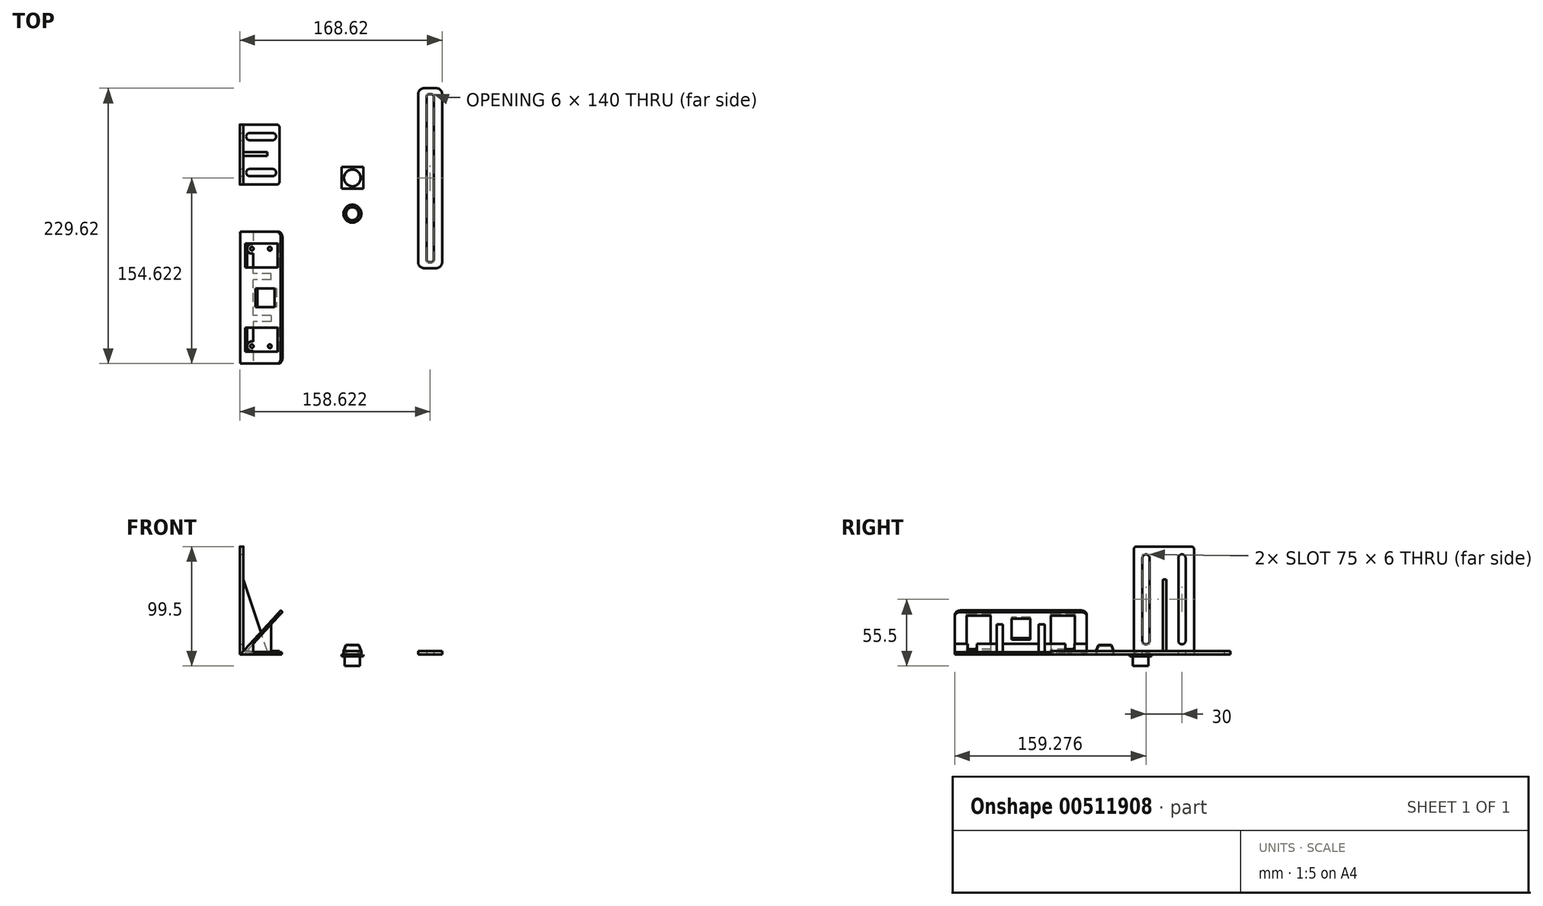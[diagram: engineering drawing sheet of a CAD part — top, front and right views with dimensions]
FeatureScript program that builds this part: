
annotation { "Feature Type Name" : "Feature", "Feature Type Description" : "" }
export const myFeature = defineFeature(function(context is Context, id is Id, definition is map)
    precondition{}
    {
        {
            var Q0;
            Q0=qCreatedBy(makeId("Top.planeOp"),FACE);
            var sketch = newSketch(context, id + "F0", { "sketchPlane" : qUnion([Q0])});
            skCircle(sketch, "E0", {"center": v(0, 0) * mm, "radius": 7 * mm});
            skSolve(sketch);
        }
        {
            var Q0;
            Q0=makeQuery(id+"F0.imprint","IMPRINT",FACE,{"disambiguationData":[TD([[makeQuery(id+"F0.imprint","IMPRINT",EDGE,{"derivedFrom":sQuery(id+"F0.wireOp",EDGE,"E0")}),1.0]])]});
            extrude(context, id + "F1", {"entities" : qUnion([Q0]), "depth" : 2.5 * mm, "offsetDistance" : 25 * mm});
        }
        {
            var Q0;
            Q0=makeQuery(id+"F1.opExtrude","CAP_EDGE",EDGE,{"disambiguationData":[OSD([sQuery(id+"F0.wireOp",EDGE,"E0")])],"isStart":false});
            fillet(context, id + "F2", {"entities" : qUnion([Q0]), "radius" : 7 * mm, "tangentPropagation" : true, "allowEdgeOverflow" : false});
        }
        {
            var Q0;
            Q0=makeQuery(id+"F1.opExtrude","CAP_FACE",FACE,{"disambiguationData":[OSD([sQuery(id+"F0.wireOp",EDGE,"E0")])],"isStart":true});
            cPlane(context, id + "F3", {"entities" : qUnion([Q0]), "cplaneType" : CPlaneType.OFFSET, "offset" : 0 * mm, "width" : 150 * mm, "height" : 150 * mm});
        }
        {
            var Q0;
            Q0=qCreatedBy(id+"F3.planeOp",FACE);
            var sketch = newSketch(context, id + "F4", { "sketchPlane" : qUnion([Q0])});
            skLineSegment(sketch, "E1.bottom", {"start": v(-9, -9) * mm, "end": v(9, -9) * mm});
            skLineSegment(sketch, "E1.top", {"start": v(-9, 9) * mm, "end": v(9, 9) * mm});
            skLineSegment(sketch, "E1.left", {"start": v(-9, -9) * mm, "end": v(-9, 9) * mm});
            skLineSegment(sketch, "E1.right", {"start": v(9, -9) * mm, "end": v(9, 9) * mm});
            skSolve(sketch);
        }
        {
            var Q0;
            Q0 = qSketchRegion(id + "F4", true);
            extrude(context, id + "F5", {"entities" : qUnion([Q0]), "operationType" : NewBodyOperationType.ADD, "depth" : 1.5 * mm, "offsetDistance" : 25 * mm});
        }
        {
            var Q0;
            Q0=makeQuery(id+"F5.opExtrude","CAP_FACE",FACE,{"disambiguationData":[OSD([sQuery(id+"F4.wireOp",EDGE,"E1.bottom"),sQuery(id+"F4.wireOp",EDGE,"E1.top"),sQuery(id+"F4.wireOp",EDGE,"E1.left"),sQuery(id+"F4.wireOp",EDGE,"E1.right")])],"isStart":false});
            cPlane(context, id + "F6", {"entities" : qUnion([Q0]), "cplaneType" : CPlaneType.OFFSET, "offset" : 0 * mm, "width" : 150 * mm, "height" : 150 * mm});
        }
        {
            var Q0;
            Q0=qCreatedBy(id+"F6.planeOp",FACE);
            var sketch = newSketch(context, id + "F7", { "sketchPlane" : qUnion([Q0])});
            skCircle(sketch, "E2", {"center": v(0, 0) * mm, "radius": 6.4 * mm});
            skSolve(sketch);
        }
        {
            var Q0;
            Q0 = qSketchRegion(id + "F7", true);
            extrude(context, id + "F8", {"entities" : qUnion([Q0]), "operationType" : NewBodyOperationType.ADD, "depth" : 8 * mm, "offsetDistance" : 25 * mm});
        }
        {
            var Q0;
            Q0=qCreatedBy(makeId("Top.planeOp"),FACE);
            var sketch = newSketch(context, id + "F9", { "sketchPlane" : qUnion([Q0])});
            skCircle(sketch, "E3", {"center": v(0, -29.84) * mm, "radius": 7.45 * mm});
            skSolve(sketch);
        }
        {
            var Q0;
            Q0 = qSketchRegion(id + "F9", true);
            extrude(context, id + "F10", {"entities" : qUnion([Q0]), "depth" : 8 * mm, "offsetDistance" : 25 * mm});
        }
        {
            var Q0;
            Q0=makeQuery(id+"F10.opExtrude","CAP_EDGE",EDGE,{"disambiguationData":[OSD([sQuery(id+"F9.wireOp",EDGE,"E3")])],"isStart":false});
            chamfer(context, id + "F11", {"entities" : qUnion([Q0]), "chamferType" : ChamferType.TWO_OFFSETS, "width1" : 2 * mm, "oppositeDirection" : false, "width2" : 5 * mm, "tangentPropagation" : true});
        }
        {
            var Q0;
            Q0=qCreatedBy(makeId("Top.planeOp"),FACE);
            var sketch = newSketch(context, id + "F12", { "sketchPlane" : qUnion([Q0])});
            skCircle(sketch, "E4", {"center": v(0, -29.84) * mm, "radius": 6.45 * mm});
            skSolve(sketch);
        }
        {
            var Q0;
            Q0 = qSketchRegion(id + "F12", true);
            extrude(context, id + "F13", {"entities" : qUnion([Q0]), "depth" : 7 * mm, "offsetDistance" : 25 * mm});
        }
        {
            var Q0;
            Q0=makeQuery(id+"F13.opExtrude","CAP_EDGE",EDGE,{"disambiguationData":[OSD([sQuery(id+"F12.wireOp",EDGE,"E4")])],"isStart":false});
            chamfer(context, id + "F14", {"entities" : qUnion([Q0]), "chamferType" : ChamferType.TWO_OFFSETS, "width1" : 1.7 * mm, "oppositeDirection" : false, "width2" : 4 * mm, "tangentPropagation" : true});
        }
        {
            var Q0;
            Q0=makeQuery(id+"F13.opExtrude","SWEPT_BODY",BODY,{"disambiguationData":[OSD([sQuery(id+"F12.wireOp",EDGE,"E4")])]});
            var Q1;
            Q1=makeQuery(id+"F10.opExtrude","SWEPT_BODY",BODY,{"disambiguationData":[OSD([sQuery(id+"F9.wireOp",EDGE,"E3")])]});
            booleanBodies(context, id + "F15", {"operationType" : BooleanOperationType.SUBTRACTION, "tools" : qUnion([Q0]), "targets" : qUnion([Q1])});
        }
        {
            var Q0;
            Q0=qCreatedBy(makeId("Top.planeOp"),FACE);
            var sketch = newSketch(context, id + "F16", { "sketchPlane" : qUnion([Q0])});
            skLineSegment(sketch, "E5.bottom", {"start": v(59.8, 74.78) * mm, "end": v(69.8, 74.78) * mm});
            skLineSegment(sketch, "E5.top", {"start": v(59.8, -75.22) * mm, "end": v(69.8, -75.22) * mm});
            skLineSegment(sketch, "E5.left", {"start": v(54.8, 69.78) * mm, "end": v(54.8, -70.22) * mm});
            skLineSegment(sketch, "E5.right", {"start": v(74.8, 69.78) * mm, "end": v(74.8, -70.22) * mm});
            skPoint(sketch, "E6.visualSharp", {"position": v(54.8, 74.78) * mm});
            skArc(sketch, "E6.filletArc", {"start": v(59.8, 74.78) * mm, "mid": v(56.27, 73.32) * mm, "end": v(54.8, 69.78) * mm});
            skPoint(sketch, "E7.visualSharp", {"position": v(74.8, 74.78) * mm});
            skArc(sketch, "E7.filletArc", {"start": v(74.8, 69.78) * mm, "mid": v(73.34, 73.32) * mm, "end": v(69.8, 74.78) * mm});
            skPoint(sketch, "E8.visualSharp", {"position": v(54.8, -75.22) * mm});
            skArc(sketch, "E8.filletArc", {"start": v(54.8, -70.22) * mm, "mid": v(56.27, -73.75) * mm, "end": v(59.8, -75.22) * mm});
            skPoint(sketch, "E9.visualSharp", {"position": v(74.8, -75.22) * mm});
            skArc(sketch, "E9.filletArc", {"start": v(69.8, -75.22) * mm, "mid": v(73.34, -73.75) * mm, "end": v(74.8, -70.22) * mm});
            skLineSegment(sketch, "E10.bottom", {"start": v(63.8, 69.78) * mm, "end": v(65.8, 69.78) * mm});
            skLineSegment(sketch, "E10.top", {"start": v(63.8, -70.22) * mm, "end": v(65.8, -70.22) * mm});
            skLineSegment(sketch, "E10.left", {"start": v(61.8, 67.78) * mm, "end": v(61.8, -68.22) * mm});
            skLineSegment(sketch, "E10.right", {"start": v(67.8, 67.78) * mm, "end": v(67.8, -68.22) * mm});
            skPoint(sketch, "E11.visualSharp", {"position": v(61.8, 69.78) * mm});
            skArc(sketch, "E11.filletArc", {"start": v(63.8, 69.78) * mm, "mid": v(62.39, 69.2) * mm, "end": v(61.8, 67.78) * mm});
            skPoint(sketch, "E12.visualSharp", {"position": v(61.8, -70.22) * mm});
            skArc(sketch, "E12.filletArc", {"start": v(61.8, -68.22) * mm, "mid": v(62.39, -69.63) * mm, "end": v(63.8, -70.22) * mm});
            skPoint(sketch, "E13.visualSharp", {"position": v(67.8, -70.22) * mm});
            skArc(sketch, "E13.filletArc", {"start": v(65.8, -70.22) * mm, "mid": v(67.22, -69.63) * mm, "end": v(67.8, -68.22) * mm});
            skPoint(sketch, "E14.visualSharp", {"position": v(67.8, 69.78) * mm});
            skArc(sketch, "E14.filletArc", {"start": v(67.8, 67.78) * mm, "mid": v(67.22, 69.2) * mm, "end": v(65.8, 69.78) * mm});
            skSolve(sketch);
        }
        {
            var Q0;
            Q0 = qSketchRegion(id + "F16", true);
            extrude(context, id + "F17", {"entities" : qUnion([Q0]), "depth" : 3 * mm, "offsetDistance" : 25 * mm});
        }
        {
            var Q0;
            Q0=qCreatedBy(makeId("Top.planeOp"),FACE);
            var sketch = newSketch(context, id + "F18", { "sketchPlane" : qUnion([Q0])});
            skLineSegment(sketch, "E15.bottom", {"start": v(-90.82, 44.44) * mm, "end": v(-62.82, 44.44) * mm});
            skLineSegment(sketch, "E15.top", {"start": v(-90.82, -5.56) * mm, "end": v(-62.82, -5.56) * mm});
            skLineSegment(sketch, "E15.left", {"start": v(-90.82, 44.44) * mm, "end": v(-90.82, -5.56) * mm});
            skLineSegment(sketch, "E15.right", {"start": v(-60.82, 42.44) * mm, "end": v(-60.82, -3.56) * mm});
            skPoint(sketch, "E16.visualSharp", {"position": v(-60.82, 44.44) * mm});
            skArc(sketch, "E16.filletArc", {"start": v(-60.82, 42.44) * mm, "mid": v(-61.4, 43.85) * mm, "end": v(-62.82, 44.44) * mm});
            skPoint(sketch, "E17.visualSharp", {"position": v(-60.82, -5.56) * mm});
            skArc(sketch, "E17.filletArc", {"start": v(-62.82, -5.56) * mm, "mid": v(-61.4, -4.98) * mm, "end": v(-60.82, -3.56) * mm});
            skLineSegment(sketch, "E18.bottom", {"start": v(-101.44, 55.6) * mm, "end": v(-90.82, 55.6) * mm, "construction": true});
            skLineSegment(sketch, "E18.top", {"start": v(-101.44, -19.09) * mm, "end": v(-90.82, -19.09) * mm, "construction": true});
            skLineSegment(sketch, "E18.left", {"start": v(-101.44, 55.6) * mm, "end": v(-101.44, -19.09) * mm, "construction": true});
            skLineSegment(sketch, "E18.right", {"start": v(-90.82, 55.6) * mm, "end": v(-90.82, -19.09) * mm, "construction": true});
            skSolve(sketch);
        }
        {
            var Q0;
            Q0 = qSketchRegion(id + "F18", true);
            extrude(context, id + "F19", {"entities" : qUnion([Q0]), "depth" : 3 * mm, "offsetDistance" : 25 * mm});
        }
        {
            var Q0;
            Q0=qCreatedBy(makeId("Top.planeOp"),FACE);
            var sketch = newSketch(context, id + "F20", { "sketchPlane" : qUnion([Q0])});
            skLineSegment(sketch, "E19.bottom", {"start": v(-93.82, 44.44) * mm, "end": v(-90.82, 44.44) * mm});
            skLineSegment(sketch, "E19.top", {"start": v(-93.82, -5.56) * mm, "end": v(-90.82, -5.56) * mm});
            skLineSegment(sketch, "E19.left", {"start": v(-93.82, 44.44) * mm, "end": v(-93.82, -5.56) * mm});
            skLineSegment(sketch, "E19.right", {"start": v(-90.82, 44.44) * mm, "end": v(-90.82, -5.56) * mm});
            skSolve(sketch);
        }
        {
            var Q0;
            Q0 = qSketchRegion(id + "F20", true);
            extrude(context, id + "F21", {"entities" : qUnion([Q0]), "operationType" : NewBodyOperationType.ADD, "depth" : 90 * mm, "offsetDistance" : 25 * mm});
        }
        {
            var Q0;
            Q0=makeQuery(id+"F21.opExtrude","CAP_EDGE",EDGE,{"disambiguationData":[OSD([sQuery(id+"F20.wireOp",EDGE,"E19.top")])],"isStart":false});
            var Q1;
            Q1=makeQuery(id+"F21.opExtrude","CAP_EDGE",EDGE,{"disambiguationData":[OSD([sQuery(id+"F20.wireOp",EDGE,"E19.bottom")])],"isStart":false});
            fillet(context, id + "F22", {"entities" : qUnion([Q0, Q1]), "radius" : 2 * mm, "tangentPropagation" : true, "allowEdgeOverflow" : false});
        }
        {
            var Q0;
            Q0=makeQuery(id+"F19.opExtrude","CAP_FACE",FACE,{"disambiguationData":[OSD([sQuery(id+"F18.wireOp",EDGE,"E15.bottom"),sQuery(id+"F18.wireOp",EDGE,"E15.top"),sQuery(id+"F18.wireOp",EDGE,"E15.left"),sQuery(id+"F18.wireOp",EDGE,"E15.right"),sQuery(id+"F18.wireOp",EDGE,"E16.filletArc"),sQuery(id+"F18.wireOp",EDGE,"E17.filletArc")])],"isStart":false});
            var sketch = newSketch(context, id + "F23", { "sketchPlane" : qUnion([Q0])});
            skLineSegment(sketch, "E20.bottom", {"start": v(-85.49, 37.44) * mm, "end": v(-66.49, 37.44) * mm});
            skLineSegment(sketch, "E20.top", {"start": v(-85.49, 31.44) * mm, "end": v(-66.49, 31.44) * mm});
            skLineSegment(sketch, "E20.left", {"start": v(-88.49, 34.44) * mm, "end": v(-88.49, 34.44) * mm});
            skLineSegment(sketch, "E20.right", {"start": v(-63.49, 34.44) * mm, "end": v(-63.49, 34.44) * mm});
            skPoint(sketch, "E21.visualSharp", {"position": v(-88.49, 37.44) * mm});
            skArc(sketch, "E21.filletArc", {"start": v(-85.49, 37.44) * mm, "mid": v(-87.6, 36.56) * mm, "end": v(-88.49, 34.44) * mm});
            skPoint(sketch, "E22.visualSharp", {"position": v(-88.49, 31.44) * mm});
            skArc(sketch, "E22.filletArc", {"start": v(-88.49, 34.44) * mm, "mid": v(-87.6, 32.31) * mm, "end": v(-85.49, 31.44) * mm});
            skPoint(sketch, "E23.visualSharp", {"position": v(-63.49, 31.44) * mm});
            skArc(sketch, "E23.filletArc", {"start": v(-66.49, 31.44) * mm, "mid": v(-64.37, 32.31) * mm, "end": v(-63.49, 34.44) * mm});
            skPoint(sketch, "E24.visualSharp", {"position": v(-63.49, 37.44) * mm});
            skArc(sketch, "E24.filletArc", {"start": v(-63.49, 34.44) * mm, "mid": v(-64.37, 36.56) * mm, "end": v(-66.49, 37.44) * mm});
            skLineSegment(sketch, "E25.bottom", {"start": v(-85.49, 7.44) * mm, "end": v(-66.49, 7.44) * mm});
            skLineSegment(sketch, "E25.top", {"start": v(-85.49, 1.44) * mm, "end": v(-66.49, 1.44) * mm});
            skLineSegment(sketch, "E25.left", {"start": v(-88.49, 4.44) * mm, "end": v(-88.49, 4.44) * mm});
            skLineSegment(sketch, "E25.right", {"start": v(-63.49, 4.44) * mm, "end": v(-63.49, 4.44) * mm});
            skPoint(sketch, "E26.visualSharp", {"position": v(-88.49, 7.44) * mm});
            skArc(sketch, "E26.filletArc", {"start": v(-85.49, 7.44) * mm, "mid": v(-87.61, 6.56) * mm, "end": v(-88.49, 4.44) * mm});
            skPoint(sketch, "E27.visualSharp", {"position": v(-88.49, 1.44) * mm});
            skArc(sketch, "E27.filletArc", {"start": v(-88.49, 4.44) * mm, "mid": v(-87.61, 2.31) * mm, "end": v(-85.49, 1.44) * mm});
            skPoint(sketch, "E28.visualSharp", {"position": v(-63.49, 1.44) * mm});
            skArc(sketch, "E28.filletArc", {"start": v(-66.49, 1.44) * mm, "mid": v(-64.37, 2.31) * mm, "end": v(-63.49, 4.44) * mm});
            skPoint(sketch, "E29.visualSharp", {"position": v(-63.49, 7.44) * mm});
            skArc(sketch, "E29.filletArc", {"start": v(-63.49, 4.44) * mm, "mid": v(-64.37, 6.56) * mm, "end": v(-66.49, 7.44) * mm});
            skSolve(sketch);
        }
        {
            var Q0;
            Q0 = qSketchRegion(id + "F23", true);
            extrude(context, id + "F24", {"entities" : qUnion([Q0]), "operationType" : NewBodyOperationType.REMOVE, "oppositeDirection" : true, "depth" : 25 * mm, "offsetDistance" : 25 * mm});
        }
        {
            var Q0;
            Q0=makeQuery(id+"F21.opExtrude","SWEPT_FACE",FACE,{"disambiguationData":[OSD([sQuery(id+"F20.wireOp",EDGE,"E19.right")])]});
            var sketch = newSketch(context, id + "F25", { "sketchPlane" : qUnion([Q0])});
            skLineSegment(sketch, "E30.bottom", {"start": v(34.44, 83.5) * mm, "end": v(34.44, 83.5) * mm});
            skLineSegment(sketch, "E30.top", {"start": v(34.44, 8.5) * mm, "end": v(34.44, 8.5) * mm});
            skLineSegment(sketch, "E30.left", {"start": v(31.44, 80.5) * mm, "end": v(31.44, 11.5) * mm});
            skLineSegment(sketch, "E30.right", {"start": v(37.44, 80.5) * mm, "end": v(37.44, 11.5) * mm});
            skPoint(sketch, "E31.visualSharp", {"position": v(31.44, 83.5) * mm});
            skArc(sketch, "E31.filletArc", {"start": v(34.44, 83.5) * mm, "mid": v(32.31, 82.62) * mm, "end": v(31.44, 80.5) * mm});
            skPoint(sketch, "E32.visualSharp", {"position": v(31.44, 8.5) * mm});
            skArc(sketch, "E32.filletArc", {"start": v(31.44, 11.5) * mm, "mid": v(32.31, 9.38) * mm, "end": v(34.44, 8.5) * mm});
            skPoint(sketch, "E33.visualSharp", {"position": v(37.44, 83.5) * mm});
            skArc(sketch, "E33.filletArc", {"start": v(37.44, 80.5) * mm, "mid": v(36.56, 82.62) * mm, "end": v(34.44, 83.5) * mm});
            skPoint(sketch, "E34.visualSharp", {"position": v(37.44, 8.5) * mm});
            skArc(sketch, "E34.filletArc", {"start": v(34.44, 8.5) * mm, "mid": v(36.56, 9.38) * mm, "end": v(37.44, 11.5) * mm});
            skLineSegment(sketch, "E35.bottom", {"start": v(49.07, 61.34) * mm, "end": v(49.07, 61.34) * mm});
            skLineSegment(sketch, "E35.top", {"start": v(49.07, -13.66) * mm, "end": v(49.07, -13.66) * mm});
            skLineSegment(sketch, "E35.left", {"start": v(1.44, 80.5) * mm, "end": v(1.44, 11.5) * mm});
            skLineSegment(sketch, "E35.right", {"start": v(7.44, 80.5) * mm, "end": v(7.44, 11.5) * mm});
            skPoint(sketch, "E36.visualSharp", {"position": v(1.44, 83.5) * mm});
            skArc(sketch, "E36.filletArc", {"start": v(4.44, 83.5) * mm, "mid": v(2.31, 82.62) * mm, "end": v(1.44, 80.5) * mm});
            skPoint(sketch, "E37.visualSharp", {"position": v(1.44, 8.5) * mm});
            skArc(sketch, "E37.filletArc", {"start": v(1.44, 11.5) * mm, "mid": v(2.31, 9.38) * mm, "end": v(4.44, 8.5) * mm});
            skPoint(sketch, "E38.visualSharp", {"position": v(7.44, 83.5) * mm});
            skArc(sketch, "E38.filletArc", {"start": v(7.44, 80.5) * mm, "mid": v(6.56, 82.62) * mm, "end": v(4.44, 83.5) * mm});
            skPoint(sketch, "E39.visualSharp", {"position": v(7.44, 8.5) * mm});
            skArc(sketch, "E39.filletArc", {"start": v(4.44, 8.5) * mm, "mid": v(6.56, 9.38) * mm, "end": v(7.44, 11.5) * mm});
            skSolve(sketch);
        }
        {
            var Q0;
            Q0 = qSketchRegion(id + "F25", true);
            extrude(context, id + "F26", {"entities" : qUnion([Q0]), "operationType" : NewBodyOperationType.REMOVE, "oppositeDirection" : true, "depth" : 25 * mm, "offsetDistance" : 25 * mm});
        }
        {
            var Q0;
            Q0=makeQuery(id+"F29.boolean.opBoolean","MERGE",FACE,{"derivedFrom":[makeQuery(id+"F21.boolean.opBoolean","MERGE",FACE,{"derivedFrom":[makeQuery(id+"F19.opExtrude","SWEPT_FACE",FACE,{"disambiguationData":[OSD([sQuery(id+"F18.wireOp",EDGE,"E15.top")])]}),makeQuery(id+"F21.opExtrude","SWEPT_FACE",FACE,{"disambiguationData":[OSD([sQuery(id+"F20.wireOp",EDGE,"E19.top")])]})]}),makeQuery(id+"F29.opExtrude","CAP_FACE",FACE,{"disambiguationData":[OSD([sQuery(id+"F28.wireOp",EDGE,"E40"),sQuery(id+"F28.wireOp",EDGE,"E41"),sQuery(id+"F28.wireOp",EDGE,"E42")])],"isStart":true})]});
            cPlane(context, id + "F27", {"entities" : qUnion([Q0]), "cplaneType" : CPlaneType.OFFSET, "offset" : 24 * mm, "oppositeDirection" : true, "width" : 150 * mm, "height" : 150 * mm});
        }
        {
            var Q0;
            Q0=qCreatedBy(id+"F27.planeOp",FACE);
            var sketch = newSketch(context, id + "F28", { "sketchPlane" : qUnion([Q0])});
            skLineSegment(sketch, "E40", {"start": v(-90.82, 62.64) * mm, "end": v(-90.82, 3) * mm});
            skLineSegment(sketch, "E41", {"start": v(-90.82, 3) * mm, "end": v(-70.95, 3) * mm});
            skLineSegment(sketch, "E42", {"start": v(-70.95, 3) * mm, "end": v(-90.82, 62.64) * mm});
            skSolve(sketch);
        }
        {
            var Q0;
            Q0=makeQuery(id+"F28.imprint","IMPRINT",FACE,{"disambiguationData":[TD([[makeQuery(id+"F28.imprint","IMPRINT",EDGE,{"derivedFrom":sQuery(id+"F28.wireOp",EDGE,"E40")}),1.0]])]});
            extrude(context, id + "F29", {"entities" : qUnion([Q0]), "operationType" : NewBodyOperationType.ADD, "oppositeDirection" : true, "depth" : 3 * mm, "offsetDistance" : 25 * mm});
        }
        {
            var Q0;
            Q0=qCreatedBy(makeId("Top.planeOp"),FACE);
            var sketch = newSketch(context, id + "F30", { "sketchPlane" : qUnion([Q0])});
            skLineSegment(sketch, "E43.bottom", {"start": v(-88.77, -44.84) * mm, "end": v(-63.77, -44.84) * mm});
            skLineSegment(sketch, "E43.top", {"start": v(-88.77, -154.84) * mm, "end": v(-63.77, -154.84) * mm});
            skLineSegment(sketch, "E43.left", {"start": v(-88.77, -44.84) * mm, "end": v(-88.77, -154.84) * mm});
            skLineSegment(sketch, "E43.right", {"start": v(-58.77, -49.84) * mm, "end": v(-58.77, -149.84) * mm});
            skPoint(sketch, "E44.visualSharp", {"position": v(-58.77, -44.84) * mm});
            skArc(sketch, "E44.filletArc", {"start": v(-58.77, -49.84) * mm, "mid": v(-60.23, -46.3) * mm, "end": v(-63.77, -44.84) * mm});
            skPoint(sketch, "E45.visualSharp", {"position": v(-58.77, -154.84) * mm});
            skArc(sketch, "E45.filletArc", {"start": v(-63.77, -154.84) * mm, "mid": v(-60.23, -153.38) * mm, "end": v(-58.77, -149.84) * mm});
            skSolve(sketch);
        }
        {
            var Q0;
            Q0 = qSketchRegion(id + "F30", true);
            extrude(context, id + "F31", {"entities" : qUnion([Q0]), "depth" : 2 * mm, "offsetDistance" : 25 * mm});
        }
        {
            var Q0;
            Q0=makeQuery(id+"F31.opExtrude","SWEPT_FACE",FACE,{"disambiguationData":[OSD([sQuery(id+"F30.wireOp",EDGE,"E43.top")])]});
            var sketch = newSketch(context, id + "F32", { "sketchPlane" : qUnion([Q0])});
            skLineSegment(sketch, "E46", {"start": v(-88.77, 2) * mm, "end": v(-58.2, 35.45) * mm});
            skLineSegment(sketch, "E47", {"start": v(-58.2, 35.45) * mm, "end": v(-59.67, 36.8) * mm});
            skLineSegment(sketch, "E48", {"start": v(-59.67, 36.8) * mm, "end": v(-93.3, 0) * mm});
            skLineSegment(sketch, "E49", {"start": v(-93.3, 0) * mm, "end": v(-88.77, 0) * mm});
            skLineSegment(sketch, "E50", {"start": v(-88.77, 0) * mm, "end": v(-88.77, 2) * mm});
            skSolve(sketch);
        }
        {
            var Q0;
            Q0 = qSketchRegion(id + "F32", true);
            extrude(context, id + "F33", {"entities" : qUnion([Q0]), "operationType" : NewBodyOperationType.ADD, "oppositeDirection" : true, "depth" : 110 * mm, "offsetDistance" : 25 * mm});
        }
        {
            var Q0;
            Q0=makeQuery(id+"F33.opExtrude","CAP_EDGE",EDGE,{"disambiguationData":[OSD([sQuery(id+"F32.wireOp",EDGE,"E47")])],"isStart":true});
            var Q1;
            Q1=makeQuery(id+"F33.opExtrude","CAP_EDGE",EDGE,{"disambiguationData":[OSD([sQuery(id+"F32.wireOp",EDGE,"E47")])],"isStart":false});
            fillet(context, id + "F34", {"entities" : qUnion([Q0, Q1]), "radius" : 5 * mm, "tangentPropagation" : true, "allowEdgeOverflow" : false});
        }
        {
            var Q0;
            Q0=makeQuery(id+"F33.boolean.opBoolean","MERGE",FACE,{"derivedFrom":[makeQuery(id+"F31.opExtrude","SWEPT_FACE",FACE,{"disambiguationData":[OSD([sQuery(id+"F30.wireOp",EDGE,"E43.top")])]}),makeQuery(id+"F33.opExtrude","CAP_FACE",FACE,{"disambiguationData":[OSD([sQuery(id+"F32.wireOp",EDGE,"E46"),sQuery(id+"F32.wireOp",EDGE,"E47"),sQuery(id+"F32.wireOp",EDGE,"E48"),sQuery(id+"F32.wireOp",EDGE,"E49"),sQuery(id+"F32.wireOp",EDGE,"E50")])],"isStart":true})]});
            var sketch = newSketch(context, id + "F35", { "sketchPlane" : qUnion([Q0])});
            skLineSegment(sketch, "E51", {"start": v(-88.77, 2) * mm, "end": v(-82.5, 8.86) * mm});
            skLineSegment(sketch, "E52", {"start": v(-82.5, 8.86) * mm, "end": v(-82.5, 2) * mm});
            skLineSegment(sketch, "E53", {"start": v(-82.5, 2) * mm, "end": v(-88.77, 2) * mm});
            skSolve(sketch);
        }
        {
            var Q0;
            Q0 = qSketchRegion(id + "F35", true);
            extrude(context, id + "F36", {"entities" : qUnion([Q0]), "operationType" : NewBodyOperationType.ADD, "oppositeDirection" : true, "depth" : 110 * mm, "offsetDistance" : 25 * mm});
        }
        {
            var Q0;
            Q0=qCreatedBy(makeId("Top.planeOp"),FACE);
            cPlane(context, id + "F37", {"entities" : qUnion([Q0]), "cplaneType" : CPlaneType.OFFSET, "offset" : 50 * mm, "width" : 150 * mm, "height" : 150 * mm});
        }
        {
            var Q0;
            Q0=qCreatedBy(id+"F37.planeOp",FACE);
            var sketch = newSketch(context, id + "F38", { "sketchPlane" : qUnion([Q0])});
            skPoint(sketch, "E54", {"position": v(-68.77, -59.07) * mm});
            skPoint(sketch, "E55", {"position": v(-83.77, -59.07) * mm});
            skPoint(sketch, "E56", {"position": v(-68.77, -140.34) * mm});
            skPoint(sketch, "E57", {"position": v(-83.77, -140.34) * mm});
            skSolve(sketch);
        }
        {
            var Q0;
            Q0=sQuery(id+"F38.wireOp",VERTEX,"E57");
            var Q1;
            Q1=sQuery(id+"F38.wireOp",VERTEX,"E56");
            var Q2;
            Q2=sQuery(id+"F38.wireOp",VERTEX,"E55");
            var Q3;
            Q3=sQuery(id+"F38.wireOp",VERTEX,"E54");
            var Q4;
            Q4=makeQuery(id+"F31.opExtrude","SWEPT_BODY",BODY,{"disambiguationData":[OSD([sQuery(id+"F30.wireOp",EDGE,"E43.bottom"),sQuery(id+"F30.wireOp",EDGE,"E43.top"),sQuery(id+"F30.wireOp",EDGE,"E43.left"),sQuery(id+"F30.wireOp",EDGE,"E43.right"),sQuery(id+"F30.wireOp",EDGE,"E44.filletArc"),sQuery(id+"F30.wireOp",EDGE,"E45.filletArc")])]});
            hole(context, id + "F39", {"style" : HoleStyle.SIMPLE, "endStyle" : HoleEndStyle.BLIND, "holeDiameter" : 3 * mm, "holeDepth" : 50 * mm, "tappedDepth" : 12 * mm, "tapClearance" : 3, "locations" : qUnion([Q0, Q1, Q2, Q3]), "scope" : qUnion([Q4])});
        }
        {
            var Q0;
            Q0=qCreatedBy(id+"F37.planeOp",FACE);
            var sketch = newSketch(context, id + "F40", { "sketchPlane" : qUnion([Q0])});
            skPoint(sketch, "E58", {"position": v(-68.77, -59.07) * mm});
            skPoint(sketch, "E59", {"position": v(-83.77, -59.07) * mm});
            skPoint(sketch, "E60", {"position": v(-68.77, -140.34) * mm});
            skPoint(sketch, "E61", {"position": v(-83.77, -140.34) * mm});
            skSolve(sketch);
        }
        {
            var Q0;
            Q0=sQuery(id+"F40.wireOp",VERTEX,"E61");
            var Q1;
            Q1=sQuery(id+"F40.wireOp",VERTEX,"E60");
            var Q2;
            Q2=sQuery(id+"F40.wireOp",VERTEX,"E58");
            var Q3;
            Q3=sQuery(id+"F40.wireOp",VERTEX,"E59");
            var Q4;
            Q4=makeQuery(id+"F31.opExtrude","SWEPT_BODY",BODY,{"disambiguationData":[OSD([sQuery(id+"F30.wireOp",EDGE,"E43.bottom"),sQuery(id+"F30.wireOp",EDGE,"E43.top"),sQuery(id+"F30.wireOp",EDGE,"E43.left"),sQuery(id+"F30.wireOp",EDGE,"E43.right"),sQuery(id+"F30.wireOp",EDGE,"E44.filletArc"),sQuery(id+"F30.wireOp",EDGE,"E45.filletArc")])]});
            hole(context, id + "F41", {"style" : HoleStyle.SIMPLE, "endStyle" : HoleEndStyle.BLIND, "holeDiameter" : 8 * mm, "holeDepth" : 19 * mm, "tappedDepth" : 12 * mm, "tapClearance" : 3, "locations" : qUnion([Q0, Q1, Q2, Q3]), "scope" : qUnion([Q4])});
        }
        {
            var Q0;
            Q0=makeQuery(id+"F33.boolean.opBoolean","MERGE",FACE,{"derivedFrom":[makeQuery(id+"F31.opExtrude","CAP_FACE",FACE,{"disambiguationData":[OSD([sQuery(id+"F30.wireOp",EDGE,"E43.bottom"),sQuery(id+"F30.wireOp",EDGE,"E43.top"),sQuery(id+"F30.wireOp",EDGE,"E43.left"),sQuery(id+"F30.wireOp",EDGE,"E43.right"),sQuery(id+"F30.wireOp",EDGE,"E44.filletArc"),sQuery(id+"F30.wireOp",EDGE,"E45.filletArc")])],"isStart":true}),makeQuery(id+"F33.opExtrude","SWEPT_FACE",FACE,{"disambiguationData":[OSD([sQuery(id+"F32.wireOp",EDGE,"E49")])]})]});
            var sketch = newSketch(context, id + "F42", { "sketchPlane" : qUnion([Q0])});
            skCircle(sketch, "E62", {"center": v(-83.77, 59.07) * mm, "radius": 4 * mm});
            skCircle(sketch, "E63", {"center": v(-83.77, 140.34) * mm, "radius": 4 * mm});
            skSolve(sketch);
        }
        {
            var Q0;
            Q0 = qSketchRegion(id + "F42", true);
            extrude(context, id + "F43", {"entities" : qUnion([Q0]), "operationType" : NewBodyOperationType.ADD, "oppositeDirection" : true, "depth" : 2 * mm, "offsetDistance" : 25 * mm});
        }
        {
            var Q0;
            Q0=makeQuery(id+"F43.boolean.opBoolean","MERGE",FACE,{"derivedFrom":[makeQuery(id+"F31.opExtrude","CAP_FACE",FACE,{"disambiguationData":[OSD([sQuery(id+"F30.wireOp",EDGE,"E43.bottom"),sQuery(id+"F30.wireOp",EDGE,"E43.top"),sQuery(id+"F30.wireOp",EDGE,"E43.left"),sQuery(id+"F30.wireOp",EDGE,"E43.right"),sQuery(id+"F30.wireOp",EDGE,"E44.filletArc"),sQuery(id+"F30.wireOp",EDGE,"E45.filletArc")])],"isStart":false}),makeQuery(id+"F43.opExtrude","CAP_FACE",FACE,{"disambiguationData":[OSD([sQuery(id+"F42.wireOp",EDGE,"E62")])],"isStart":false}),makeQuery(id+"F43.opExtrude","CAP_FACE",FACE,{"disambiguationData":[OSD([sQuery(id+"F42.wireOp",EDGE,"E63")])],"isStart":false})]});
            var sketch = newSketch(context, id + "F44", { "sketchPlane" : qUnion([Q0])});
            skPoint(sketch, "E64", {"position": v(-83.77, -59.07) * mm});
            skPoint(sketch, "E65", {"position": v(-83.77, -140.34) * mm});
            skSolve(sketch);
        }
        {
            var Q0;
            Q0=sQuery(id+"F44.wireOp",VERTEX,"E64");
            var Q1;
            Q1=sQuery(id+"F44.wireOp",VERTEX,"E65");
            var Q2;
            Q2=makeQuery(id+"F31.opExtrude","SWEPT_BODY",BODY,{"disambiguationData":[OSD([sQuery(id+"F30.wireOp",EDGE,"E43.bottom"),sQuery(id+"F30.wireOp",EDGE,"E43.top"),sQuery(id+"F30.wireOp",EDGE,"E43.left"),sQuery(id+"F30.wireOp",EDGE,"E43.right"),sQuery(id+"F30.wireOp",EDGE,"E44.filletArc"),sQuery(id+"F30.wireOp",EDGE,"E45.filletArc")])]});
            hole(context, id + "F45", {"style" : HoleStyle.SIMPLE, "endStyle" : HoleEndStyle.BLIND, "holeDiameter" : 3 * mm, "holeDepth" : 19 * mm, "tappedDepth" : 12 * mm, "tapClearance" : 3, "locations" : qUnion([Q0, Q1]), "scope" : qUnion([Q2])});
        }
        {
            var Q0;
            Q0=makeQuery(id+"F33.opExtrude","SWEPT_FACE",FACE,{"disambiguationData":[OSD([sQuery(id+"F32.wireOp",EDGE,"E48")])]});
            cPlane(context, id + "F46", {"entities" : qUnion([Q0]), "cplaneType" : CPlaneType.OFFSET, "offset" : 25 * mm, "width" : 150 * mm, "height" : 150 * mm});
        }
        {
            var Q0;
            Q0=qCreatedBy(id+"F46.planeOp",FACE);
            var sketch = newSketch(context, id + "F47", { "sketchPlane" : qUnion([Q0])});
            skLineSegment(sketch, "E66.bottom", {"start": v(54.84, -16.95) * mm, "end": v(74.84, -16.95) * mm});
            skLineSegment(sketch, "E66.top", {"start": v(54.84, -56.95) * mm, "end": v(74.84, -56.95) * mm});
            skLineSegment(sketch, "E66.left", {"start": v(54.84, -16.95) * mm, "end": v(54.84, -56.95) * mm});
            skLineSegment(sketch, "E66.right", {"start": v(74.84, -16.95) * mm, "end": v(74.84, -56.95) * mm});
            skLineSegment(sketch, "E67.bottom", {"start": v(124.84, -16.95) * mm, "end": v(144.84, -16.95) * mm});
            skLineSegment(sketch, "E67.top", {"start": v(124.84, -56.95) * mm, "end": v(144.84, -56.95) * mm});
            skLineSegment(sketch, "E67.left", {"start": v(124.84, -16.95) * mm, "end": v(124.84, -56.95) * mm});
            skLineSegment(sketch, "E67.right", {"start": v(144.84, -16.95) * mm, "end": v(144.84, -56.95) * mm});
            skLineSegment(sketch, "E68.bottom", {"start": v(92.04, -20.68) * mm, "end": v(107.66, -20.68) * mm});
            skLineSegment(sketch, "E68.top", {"start": v(92.04, -44.21) * mm, "end": v(107.66, -44.21) * mm});
            skLineSegment(sketch, "E68.left", {"start": v(92.04, -20.68) * mm, "end": v(92.04, -44.21) * mm});
            skLineSegment(sketch, "E68.right", {"start": v(107.66, -20.68) * mm, "end": v(107.66, -44.21) * mm});
            skSolve(sketch);
        }
        {
            var Q0;
            Q0 = qSketchRegion(id + "F47", true);
            extrude(context, id + "F48", {"entities" : qUnion([Q0]), "operationType" : NewBodyOperationType.REMOVE, "oppositeDirection" : true, "depth" : 27 * mm, "offsetDistance" : 25 * mm});
        }
        {
            var Q0;
            Q0=makeQuery(id+"F36.boolean.opBoolean","MERGE",FACE,{"derivedFrom":[makeQuery(id+"F33.boolean.opBoolean","MERGE",FACE,{"derivedFrom":[makeQuery(id+"F31.opExtrude","SWEPT_FACE",FACE,{"disambiguationData":[OSD([sQuery(id+"F30.wireOp",EDGE,"E43.top")])]}),makeQuery(id+"F33.opExtrude","CAP_FACE",FACE,{"disambiguationData":[OSD([sQuery(id+"F32.wireOp",EDGE,"E46"),sQuery(id+"F32.wireOp",EDGE,"E47"),sQuery(id+"F32.wireOp",EDGE,"E48"),sQuery(id+"F32.wireOp",EDGE,"E49"),sQuery(id+"F32.wireOp",EDGE,"E50")])],"isStart":true})]}),makeQuery(id+"F36.opExtrude","CAP_FACE",FACE,{"disambiguationData":[OSD([sQuery(id+"F35.wireOp",EDGE,"E51"),sQuery(id+"F35.wireOp",EDGE,"E52"),sQuery(id+"F35.wireOp",EDGE,"E53")])],"isStart":true})]});
            cPlane(context, id + "F49", {"entities" : qUnion([Q0]), "cplaneType" : CPlaneType.OFFSET, "offset" : 35 * mm, "oppositeDirection" : true, "width" : 150 * mm, "height" : 150 * mm});
        }
        {
            var Q0;
            Q0=makeQuery(id+"F36.boolean.opBoolean","MERGE",FACE,{"derivedFrom":[makeQuery(id+"F33.boolean.opBoolean","MERGE",FACE,{"derivedFrom":[makeQuery(id+"F31.opExtrude","SWEPT_FACE",FACE,{"disambiguationData":[OSD([sQuery(id+"F30.wireOp",EDGE,"E43.bottom")])]}),makeQuery(id+"F33.opExtrude","CAP_FACE",FACE,{"disambiguationData":[OSD([sQuery(id+"F32.wireOp",EDGE,"E46"),sQuery(id+"F32.wireOp",EDGE,"E47"),sQuery(id+"F32.wireOp",EDGE,"E48"),sQuery(id+"F32.wireOp",EDGE,"E49"),sQuery(id+"F32.wireOp",EDGE,"E50")])],"isStart":false})]}),makeQuery(id+"F36.opExtrude","CAP_FACE",FACE,{"disambiguationData":[OSD([sQuery(id+"F35.wireOp",EDGE,"E51"),sQuery(id+"F35.wireOp",EDGE,"E52"),sQuery(id+"F35.wireOp",EDGE,"E53")])],"isStart":false})]});
            cPlane(context, id + "F50", {"entities" : qUnion([Q0]), "cplaneType" : CPlaneType.OFFSET, "offset" : 35 * mm, "oppositeDirection" : true, "width" : 150 * mm, "height" : 150 * mm});
        }
        {
            var Q0;
            Q0=qCreatedBy(id+"F49.planeOp",FACE);
            var sketch = newSketch(context, id + "F51", { "sketchPlane" : qUnion([Q0])});
            skLineSegment(sketch, "E69", {"start": v(-67.67, 2) * mm, "end": v(-82.5, 2) * mm});
            skLineSegment(sketch, "E70", {"start": v(-82.5, 2) * mm, "end": v(-82.5, 8.86) * mm});
            skLineSegment(sketch, "E71", {"start": v(-82.5, 8.86) * mm, "end": v(-67.67, 25.08) * mm});
            skLineSegment(sketch, "E72", {"start": v(-67.67, 25.08) * mm, "end": v(-67.67, 2) * mm});
            skSolve(sketch);
        }
        {
            var Q0;
            Q0 = qSketchRegion(id + "F51", true);
            extrude(context, id + "F52", {"entities" : qUnion([Q0]), "operationType" : NewBodyOperationType.ADD, "oppositeDirection" : true, "depth" : 5 * mm, "offsetDistance" : 25 * mm});
        }
        {
            var Q0;
            Q0=qCreatedBy(id+"F50.planeOp",FACE);
            var sketch = newSketch(context, id + "F53", { "sketchPlane" : qUnion([Q0])});
            skLineSegment(sketch, "E73.MirrorCS", {"start": v(67.67, 2) * mm, "end": v(82.5, 2) * mm});
            skLineSegment(sketch, "E74.MirrorCS", {"start": v(82.5, 2) * mm, "end": v(82.5, 8.86) * mm});
            skLineSegment(sketch, "E75.MirrorCS", {"start": v(82.5, 8.86) * mm, "end": v(67.67, 25.08) * mm});
            skLineSegment(sketch, "E76.MirrorCS", {"start": v(67.67, 25.08) * mm, "end": v(67.67, 2) * mm});
            skSolve(sketch);
        }
        {
            var Q0;
            Q0 = qSketchRegion(id + "F53", true);
            extrude(context, id + "F54", {"entities" : qUnion([Q0]), "operationType" : NewBodyOperationType.ADD, "oppositeDirection" : true, "depth" : 5 * mm, "offsetDistance" : 25 * mm});
        }
    });
